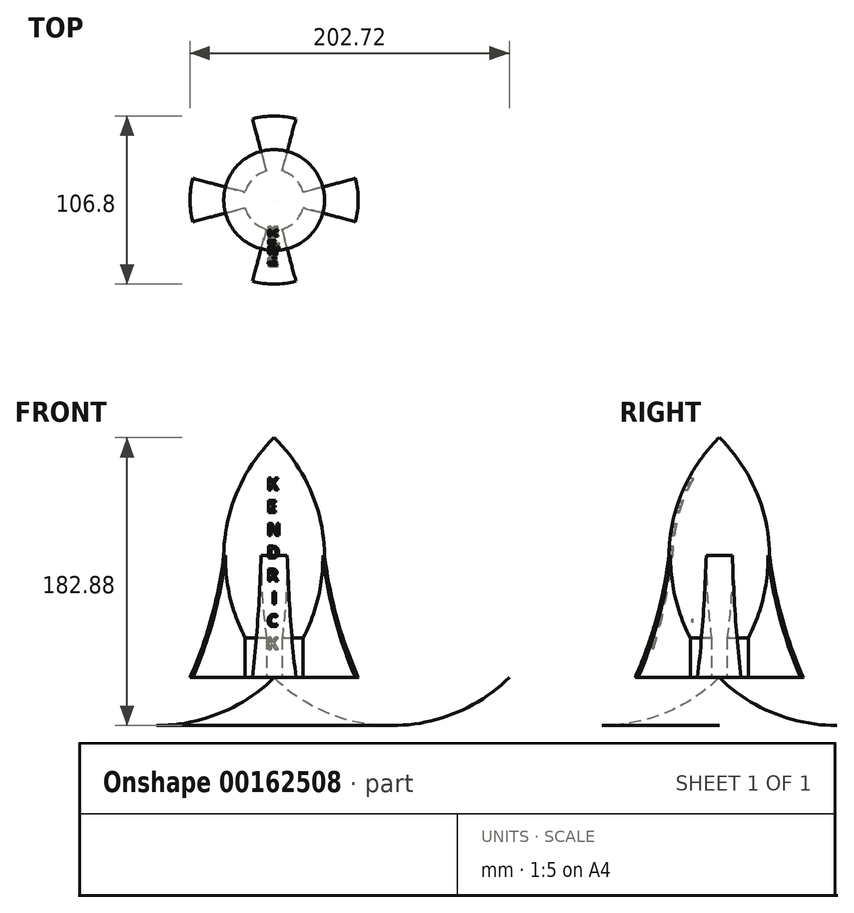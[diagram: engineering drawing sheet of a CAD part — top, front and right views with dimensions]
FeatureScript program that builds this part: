
annotation { "Feature Type Name" : "Feature", "Feature Type Description" : "" }
export const myFeature = defineFeature(function(context is Context, id is Id, definition is map)
    precondition{}
    {
        {
            var Q0;
            Q0=qCreatedBy(makeId("Front.planeOp"),FACE);
            var sketch = newSketch(context, id + "F0", { "sketchPlane" : qUnion([Q0])});
            skLineSegment(sketch, "E0", {"start": v(0, 68.83) * mm, "end": v(0, -83.57) * mm});
            skArc(sketch, "E1", {"start": v(0, 68.83) * mm, "mid": v(-32.02, -7.37) * mm, "end": v(0, -83.57) * mm});
            skLineSegment(sketch, "E2", {"start": v(0, -83.57) * mm, "end": v(-63.5, -83.57) * mm});
            skArc(sketch, "E3", {"start": v(-63.5, -83.57) * mm, "mid": v(-40.24, -48.45) * mm, "end": v(-32.02, -7.14) * mm});
            skSolve(sketch);
        }
        {
            var Q0;
            {var subQ0=sQuery(id+"F0.wireOp",EDGE,"E0");Q0=makeQuery(id+"F0.imprint","IMPRINT",FACE,{"disambiguationData":[TD([[makeQuery(id+"F0.imprint","IMPRINT",EDGE,{"derivedFrom":subQ0}),-1.0]])]});}
            var Q1;
            Q1=sQuery(id+"F0.wireOp",EDGE,"E0");
            revolve(context, id + "F1", {"entities" : qUnion([Q0]), "axis" : qUnion([Q1]), "revolveType" : RevolveType.FULL});
        }
        {
            var Q0;
            Q0=qCreatedBy(makeId("Front.planeOp"),FACE);
            var sketch = newSketch(context, id + "F2", { "sketchPlane" : qUnion([Q0])});
            skLineSegment(sketch, "E4", {"start": v(0, -83.52) * mm, "end": v(-53.4, -83.52) * mm});
            skArc(sketch, "E5", {"start": v(-53.4, -83.52) * mm, "mid": v(-39, -42.65) * mm, "end": v(-31.35, 0) * mm});
            skArc(sketch, "E6", {"start": v(-31.35, 0) * mm, "mid": v(-19.97, -43.37) * mm, "end": v(0, -83.52) * mm});
            skLineSegment(sketch, "E7", {"start": v(0, 69.5) * mm, "end": v(0, -83.52) * mm});
            skSolve(sketch);
        }
        {
            var Q0;
            Q0=makeQuery(id+"F2.imprint","IMPRINT",FACE,{"disambiguationData":[TD([[makeQuery(id+"F2.imprint","IMPRINT",EDGE,{"derivedFrom":sQuery(id+"F2.wireOp",EDGE,"E4")}),-1.0]])]});
            var Q1;
            Q1=sQuery(id+"F2.wireOp",EDGE,"E7");
            revolve(context, id + "F3", {"operationType" : NewBodyOperationType.ADD, "entities" : qUnion([Q0]), "axis" : qUnion([Q1]), "revolveType" : RevolveType.SYMMETRIC, "angle" : 30 * degree});
        }
        {
            var Q0;
            Q0=makeQuery(id+"F1.opRevolve","SWEPT_BODY",BODY,{"disambiguationData":[OSD([sQuery(id+"F0.wireOp",EDGE,"E0"),sQuery(id+"F0.wireOp",EDGE,"E1")])]});
            var Q1;
            Q1=makeQuery(id+"F1.opRevolve","SWEPT_FACE",FACE,{"disambiguationData":[OSD([sQuery(id+"F0.wireOp",EDGE,"E1")])]});
            circularPattern(context, id + "F4", {"entities" : qUnion([Q0]), "axis" : qUnion([Q1]), "angle" : 360 * degree, "instanceCount" : 4, "equalSpace" : true});
        }
        {
            var Q0;
            Q0=makeQuery(id+"F3.opRevolve","SWEPT_FACE",FACE,{"disambiguationData":[OSD([sQuery(id+"F2.wireOp",EDGE,"E4")])]});
            var sketch = newSketch(context, id + "F5", { "sketchPlane" : qUnion([Q0])});
            skCircle(sketch, "E8", {"center": v(0, 0) * mm, "radius": 19.05 * mm});
            skSolve(sketch);
        }
        {
            var Q0;
            Q0 = qSketchRegion(id + "F5", true);
            extrude(context, id + "F6", {"entities" : qUnion([Q0]), "operationType" : NewBodyOperationType.ADD, "oppositeDirection" : true, "depth" : 64 * mm});
        }
        {
            var Q0;
            Q0=qCreatedBy(makeId("Right.planeOp"),FACE);
            var sketch = newSketch(context, id + "F7", { "sketchPlane" : qUnion([Q0])});
            skArc(sketch, "E9", {"start": v(0, 65.66) * mm, "mid": v(-20.34, 35.35) * mm, "end": v(-29.47, 0) * mm});
            skArc(sketch, "E10", {"start": v(-48.32, -83.52) * mm, "mid": v(-36, -42.41) * mm, "end": v(-29.47, 0) * mm});
            skLineSegment(sketch, "E11", {"start": v(0, 65.66) * mm, "end": v(0, -83.52) * mm});
            skLineSegment(sketch, "E12", {"start": v(0, -83.52) * mm, "end": v(-48.32, -83.52) * mm});
            skSolve(sketch);
        }
        {
            var Q0;
            Q0=qCreatedBy(makeId("Front.planeOp"),FACE);
            cPlane(context, id + "F8", {"entities" : qUnion([Q0]), "cplaneType" : CPlaneType.OFFSET, "offset" : 16.9 * mm, "width" : 152.4 * mm, "height" : 152.4 * mm});
        }
        {
            var Q0;
            Q0=qCreatedBy(id+"F8.planeOp",FACE);
            var sketch = newSketch(context, id + "F9", { "sketchPlane" : qUnion([Q0])});
            skText(sketch, "E13", { "text": "K\nE\nN\nD\nR\n I\nC\nK", "fontName": "OpenSans-Bold.ttf"});
            const initialGuessF9  = {"E13": [-0.00445, 0.03568, 1, 0, 0.00766]};
            skSetInitialGuess(sketch, initialGuessF9);
            skSolve(sketch);
        }
        {
            var Q0;
            Q0 = qSketchRegion(id + "F9", true);
            extrude(context, id + "F10", {"entities" : qUnion([Q0]), "operationType" : NewBodyOperationType.REMOVE, "depth" : 25.4 * mm});
        }
        {
            var Q0;
            Q0 = qSketchRegion(id + "F7", true);
            var Q1;
            Q1=sQuery(id+"F7.wireOp",EDGE,"E11");
            revolve(context, id + "F11", {"operationType" : NewBodyOperationType.ADD, "entities" : qUnion([Q0]), "axis" : qUnion([Q1]), "revolveType" : RevolveType.SYMMETRIC, "angle" : 25 * degree});
        }
    });
